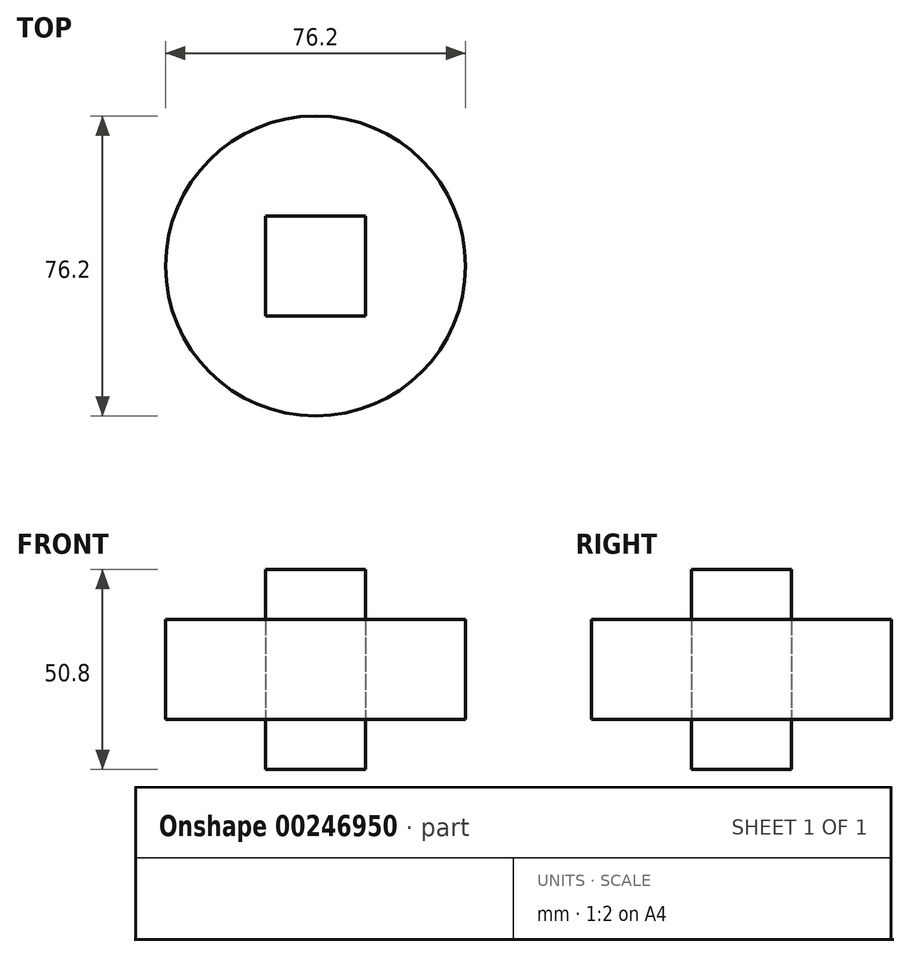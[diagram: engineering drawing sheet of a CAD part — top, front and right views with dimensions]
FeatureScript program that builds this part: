
annotation { "Feature Type Name" : "Feature", "Feature Type Description" : "" }
export const myFeature = defineFeature(function(context is Context, id is Id, definition is map)
    precondition{}
    {
        {
            var Q0;
            Q0=qCreatedBy(makeId("Top.planeOp"),FACE);
            var sketch = newSketch(context, id + "F0", { "sketchPlane" : qUnion([Q0])});
            skCircle(sketch, "E0", {"center": v(0, 0) * mm, "radius": 38.1 * mm});
            skSolve(sketch);
        }
        {
            var Q0;
            Q0=makeQuery(id+"F0.imprint","IMPRINT",FACE,{"disambiguationData":[TD([[makeQuery(id+"F0.imprint","IMPRINT",EDGE,{"derivedFrom":sQuery(id+"F0.wireOp",EDGE,"E0")}),1.0]])]});
            extrude(context, id + "F1", {"entities" : qUnion([Q0]), "endBound" : BoundingType.SYMMETRIC, "depth" : 25.4 * mm});
        }
        {
            var Q0;
            Q0=qCreatedBy(makeId("Top.planeOp"),FACE);
            var sketch = newSketch(context, id + "F2", { "sketchPlane" : qUnion([Q0])});
            skLineSegment(sketch, "E1.bottom", {"start": v(12.7, -12.7) * mm, "end": v(-12.7, -12.7) * mm});
            skLineSegment(sketch, "E1.top", {"start": v(12.7, 12.7) * mm, "end": v(-12.7, 12.7) * mm});
            skLineSegment(sketch, "E1.left", {"start": v(12.7, -12.7) * mm, "end": v(12.7, 12.7) * mm});
            skLineSegment(sketch, "E1.right", {"start": v(-12.7, -12.7) * mm, "end": v(-12.7, 12.7) * mm});
            skPoint(sketch, "E1.middle", {"position": v(0, 0) * mm});
            skSolve(sketch);
        }
        {
            var Q0;
            Q0=makeQuery(id+"F2.imprint","IMPRINT",FACE,{"disambiguationData":[TD([[makeQuery(id+"F2.imprint","IMPRINT",EDGE,{"derivedFrom":sQuery(id+"F2.wireOp",EDGE,"E1.bottom")}),-1.0]])]});
            extrude(context, id + "F3", {"entities" : qUnion([Q0]), "endBound" : BoundingType.SYMMETRIC, "depth" : 50.8 * mm});
        }
        {
            var Q0;
            Q0=makeQuery(id+"F3.opExtrude","SWEPT_BODY",BODY,{"disambiguationData":[OSD([sQuery(id+"F2.wireOp",EDGE,"E1.bottom"),sQuery(id+"F2.wireOp",EDGE,"E1.top"),sQuery(id+"F2.wireOp",EDGE,"E1.left"),sQuery(id+"F2.wireOp",EDGE,"E1.right")])]});
            var Q1;
            Q1=makeQuery(id+"F1.opExtrude","SWEPT_BODY",BODY,{"disambiguationData":[OSD([sQuery(id+"F0.wireOp",EDGE,"E0")])]});
            booleanBodies(context, id + "F4", {"operationType" : BooleanOperationType.INTERSECTION, "tools" : qUnion([Q0, Q1]), "keepTools" : true});
        }
    });
